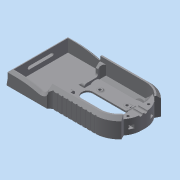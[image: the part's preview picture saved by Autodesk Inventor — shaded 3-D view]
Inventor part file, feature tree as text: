
AUTODESK INVENTOR PART (.ipt)
format: ipt  version: 2014 (Build 180170000, 170)  size: 979,456 bytes
history: native  units: in
note: dims shown in document units (in); Inventor stores cm internally (conversion verified against a paired STEP export)
features: extrude x19, sketch x19, projected_geometry x14, fillet x13, chamfer x8, plane x2, other x1, mirror x1
ambient origin geometry x8: Origin, YZ Plane, XZ Plane, XY Plane, X Axis, Y Axis, Z Axis, Center Point
bodies: Solid1 (feature_tree)
feature tree (77):
  other  "baseplate.ipt"
  extrude  "Extrusion1"  Depth=0.3937in
  extrude  "Extrusion2"  Depth=1.5in
  fillet  "Fillet2"  Radius=0.25in
  extrude  "Extrusion3"  Depth=0.125in TaperAngle=0.0deg
  extrude  "Extrusion4"  Depth=0.375in
  fillet  "Fillet3"  Radius=0.375in
  fillet  "Fillet5"  Radius=0.375in
  extrude  "Extrusion7"  Depth=0.375in
  sketch  "Sketch6"  dims[d13=0.375in d14=0.375in]
  extrude  "Extrusion9"  Depth=1.6875in
  extrude  "Extrusion14"  Depth=2.1654in
  extrude  "Extrusion21"  Depth=3.1496in
  extrude  "Extrusion22"  Depth=0.2in
  fillet  "Fillet13"  Radius=0.25in
  chamfer  "Chamfer4"  Distance=1.0in
  extrude  "Extrusion26"  Depth=0.375in
  extrude  "Extrusion27"  Depth=0.1562in
  fillet  "Fillet20"  Radius=0.201in
  extrude  "Extrusion30"  Depth=1.3742in
  fillet  "Fillet22"  Radius=1.3742in
  fillet  "Fillet23"  Radius=1.644in
  extrude  "Extrusion31"  Depth=0.2756in
  chamfer  "Chamfer6"  Distance=1.0in
  extrude  "Extrusion32"  Depth=1.0in TaperAngle=0.0deg
  chamfer  "Chamfer8"  Distance=0.125in
  extrude  "Extrusion33"  Depth=0.0394in TaperAngle=0.0deg
  plane  "Work Plane4"
  extrude  "Extrusion34"  Depth=0.0394in
  plane  "Work Plane5"
  mirror  "Mirror2"
  fillet  "Fillet24"  Radius=0.05in
  fillet  "Fillet25"  Radius=0.1in
  fillet  "Fillet26"  [1 undecoded]
  extrude  "Extrusion35"  Depth=0.0394in TaperAngle=45.0deg
  extrude  "Extrusion36"  Depth=0.0394in TaperAngle=0.0deg
  chamfer  "Chamfer10"  Distance=0.375in
  chamfer  "Chamfer11"  Distance=0.375in
  chamfer  "Chamfer12"  Distance=1.0in
  fillet  "Fillet29"  Radius=0.1875in
  chamfer  "Chamfer15"  Distance=0.75in
  chamfer  "Chamfer16"  Distance=0.125in
  extrude  "Extrusion38"  Depth=0.0394in
  fillet  "Fillet31"  Radius=0.75in
  fillet  "Fillet32"  Radius=1.0in
  sketch  "Sketch14"  dims[d24=2.1654in d25=3.1496in]
  sketch  "Sketch2"  dims[d0=0.3937in d1=3.7in]
  sketch  "Sketch3"  dims[d3=1.85in d4=1.5in d5=0.25in]
  sketch  "Sketch4"  dims[d6=0.9in d7=0.125in d8=0.0in]
  sketch  "Sketch5"  dims[d9=0.375in d10=0.375in d11=0.375in d12=0.375in]
  projected_geometry  "Projected Loop1"
  sketch  "Sketch9"  dims[d15=0.0625in d16=0.0in d21=1.6875in]
  sketch  "Sketch11"  dims[d22=4.1339in d23=2.1654in]
  sketch  "Sketch25"  dims[d27=0.25in d28=0.2in d29=0.25in]
  sketch  "Sketch29"  dims[d30=0.75in]
  projected_geometry  "Projected Loop6"
  sketch  "Sketch30"  dims[d31=0.75in d32=1.0in d33=0.0in]
  projected_geometry  "Projected Loop7"
  projected_geometry  "Projected Loop8"
  sketch  "Sketch33"  dims[d34=0.25in d35=0.0in d36=0.375in]
  projected_geometry  "Projected Loop11"
  projected_geometry  "Projected Loop12"
  sketch  "Sketch34"  dims[d37=0.4225in d39=0.1562in d50=0.201in]
  projected_geometry  "Projected Loop13"
  sketch  "Sketch35"  dims[d51=0.201in d52=1.3742in d53=1.3742in d54=1.644in]
  projected_geometry  "Projected Loop14"
  sketch  "Sketch36"  dims[d55=2.0in d56=0.0in d63=0.2756in]
  projected_geometry  "Projected Loop15"
  sketch  "Sketch37"  dims[d64=0.2756in]
  sketch  "Sketch38"  dims[d65=0.1969in]
  projected_geometry  "Projected Loop16"
  sketch  "Sketch39"  dims[d66=0.1969in d67=1.0in d68=0.0in]
  projected_geometry  "Projected Loop17"
  projected_geometry  "Projected Loop18"
  sketch  "Sketch41"  dims[d94=0.25in d95=1.0in d96=0.0in d148=0.125in d150=0.25in d151=0.0in d152=0.0625in d153=0.05in d154=0.2in d155=0.0in d156=0.0in d157=0.1in d158=0.0in d172=0.25in d173=0.125in d174=45.0deg d181=0.25in d182=0.0in d187=0.375in d188=0.375in d189=1.0in d190=0.0in d191=0.1875in d208=0.75in d209=0.125in d210=0.125in d211=0.75in d212=1.0in d213=0.0in d214=0.625in d215=0.025in d216=0.25in d217=0.0in d218=0.4375in d219=0.125in d220=45.0deg d221=0.375in d222=1.5in d223=0.0in d227=0.25in d228=0.125in d229=45.0deg d230=0.125in d231=0.25in d232=3.937in d234=0.375in d235=0.3937in d237=1.0in d239=0.03in d240=0.0in d241=-0.75in d242=0.27in d243=0.0in d247=0.5in d248=7.5in d249=0.5in d250=0.25in d251=1.5in d252=1.5in d253=0.5in d254=1.0in d255=0.0in d258=0.75in d259=0.0in d260=0.75in d261=0.125in d262=45.0deg d263=0.25in d264=0.125in d265=45.0deg d266=0.4014in d267=0.125in d268=45.0deg d269=0.0625in d279=0.1875in d280=0.125in d281=45.0deg d282=0.1875in d283=0.125in d284=45.0deg d288=0.0687in d289=0.5in d290=0.0in d291=1.0in d292=0.0394in]
  projected_geometry  "Projected Loop20"
  projected_geometry  "Projected Loop21"
note: 1 required parameter value undecoded (feature->parameter linkage not recoverable at this tier; creation-order binding heuristic only, values carry confidence <= 0.55)
